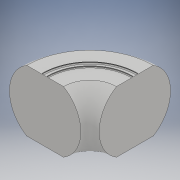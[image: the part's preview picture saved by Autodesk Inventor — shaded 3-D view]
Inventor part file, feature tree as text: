
AUTODESK INVENTOR PART (.ipt)
format: ipt  version: 2017 (Build 210142000, 142)  size: 181,248 bytes
history: native  units: in
note: dims shown in document units (in); Inventor stores cm internally (conversion verified against a paired STEP export)
features: other x1, sketch x1
ambient origin geometry x8: Origin, YZ Plane, XZ Plane, XY Plane, X Axis, Y Axis, Z Axis, Center Point
bodies: Solid1 (feature_tree)
feature tree (2):
  other  "corridor"
  sketch  "Sketch1"  dims[d1=4.0in d2=90.0deg d16=0.5833in d17=0.0625in d18=0.0625in d19=0.125in d28=45.0deg d31=3.8873in d34=2.0in d37=0.25in d38=0.125in d39=0.0892in d40=0.0884in d41=45.0deg]
